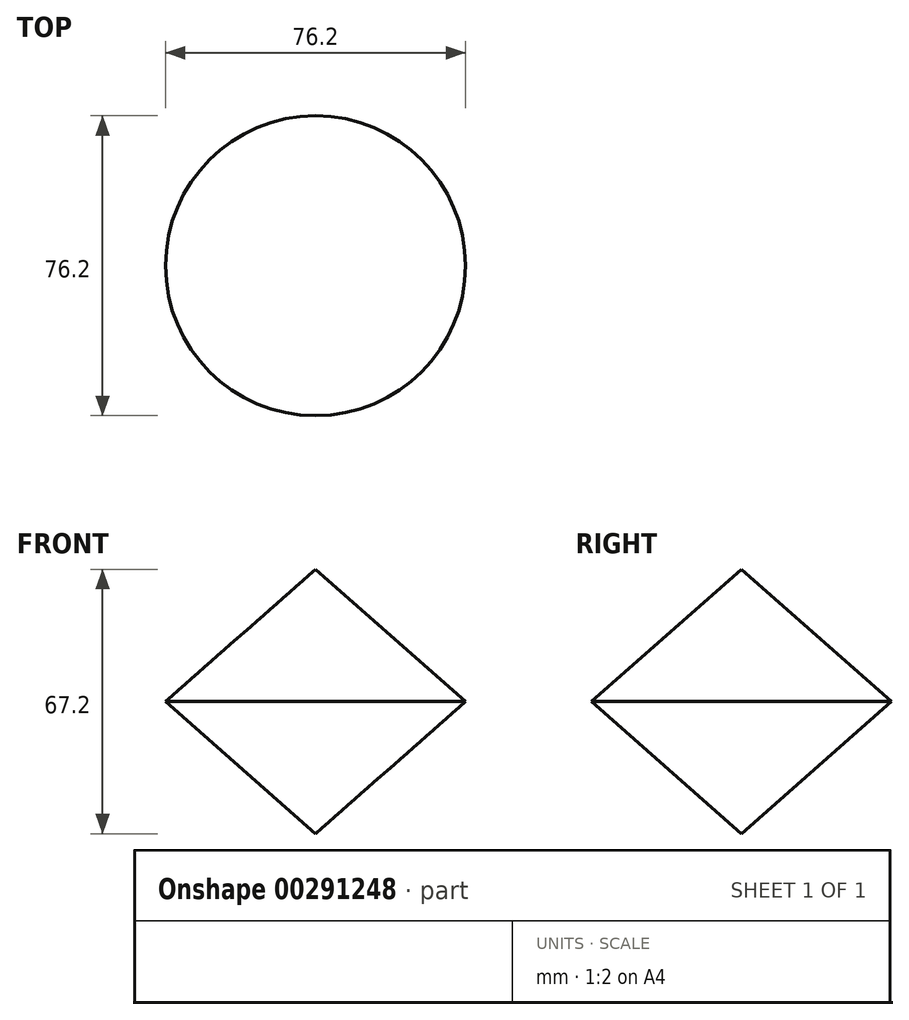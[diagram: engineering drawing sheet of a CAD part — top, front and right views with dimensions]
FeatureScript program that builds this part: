
annotation { "Feature Type Name" : "Feature", "Feature Type Description" : "" }
export const myFeature = defineFeature(function(context is Context, id is Id, definition is map)
    precondition{}
    {
        {
            var Q0;
            Q0=qCreatedBy(makeId("Front.planeOp"),FACE);
            var sketch = newSketch(context, id + "F0", { "sketchPlane" : qUnion([Q0])});
            skLineSegment(sketch, "E0", {"start": v(0, -33.6) * mm, "end": v(38.1, 0) * mm});
            skLineSegment(sketch, "E1", {"start": v(38.1, 0) * mm, "end": v(0, 33.6) * mm});
            skLineSegment(sketch, "E2", {"start": v(0, 33.6) * mm, "end": v(-38.1, 0) * mm});
            skLineSegment(sketch, "E3", {"start": v(-38.1, 0) * mm, "end": v(0, -33.6) * mm});
            skLineSegment(sketch, "E4", {"start": v(0, 63.98) * mm, "end": v(0, -71.06) * mm});
            skSolve(sketch);
        }
        {
            var Q0;
            {var subQ0=sQuery(id+"F0.wireOp",EDGE,"E0");Q0=makeQuery(id+"F0.imprint","IMPRINT",FACE,{"disambiguationData":[TD([[makeQuery(id+"F0.imprint","IMPRINT",EDGE,{"derivedFrom":subQ0}),1.0]])]});}
            var Q1;
            Q1=sQuery(id+"F0.wireOp",EDGE,"E4");
            revolve(context, id + "F1", {"entities" : qUnion([Q0]), "axis" : qUnion([Q1]), "revolveType" : RevolveType.FULL});
        }
    });
